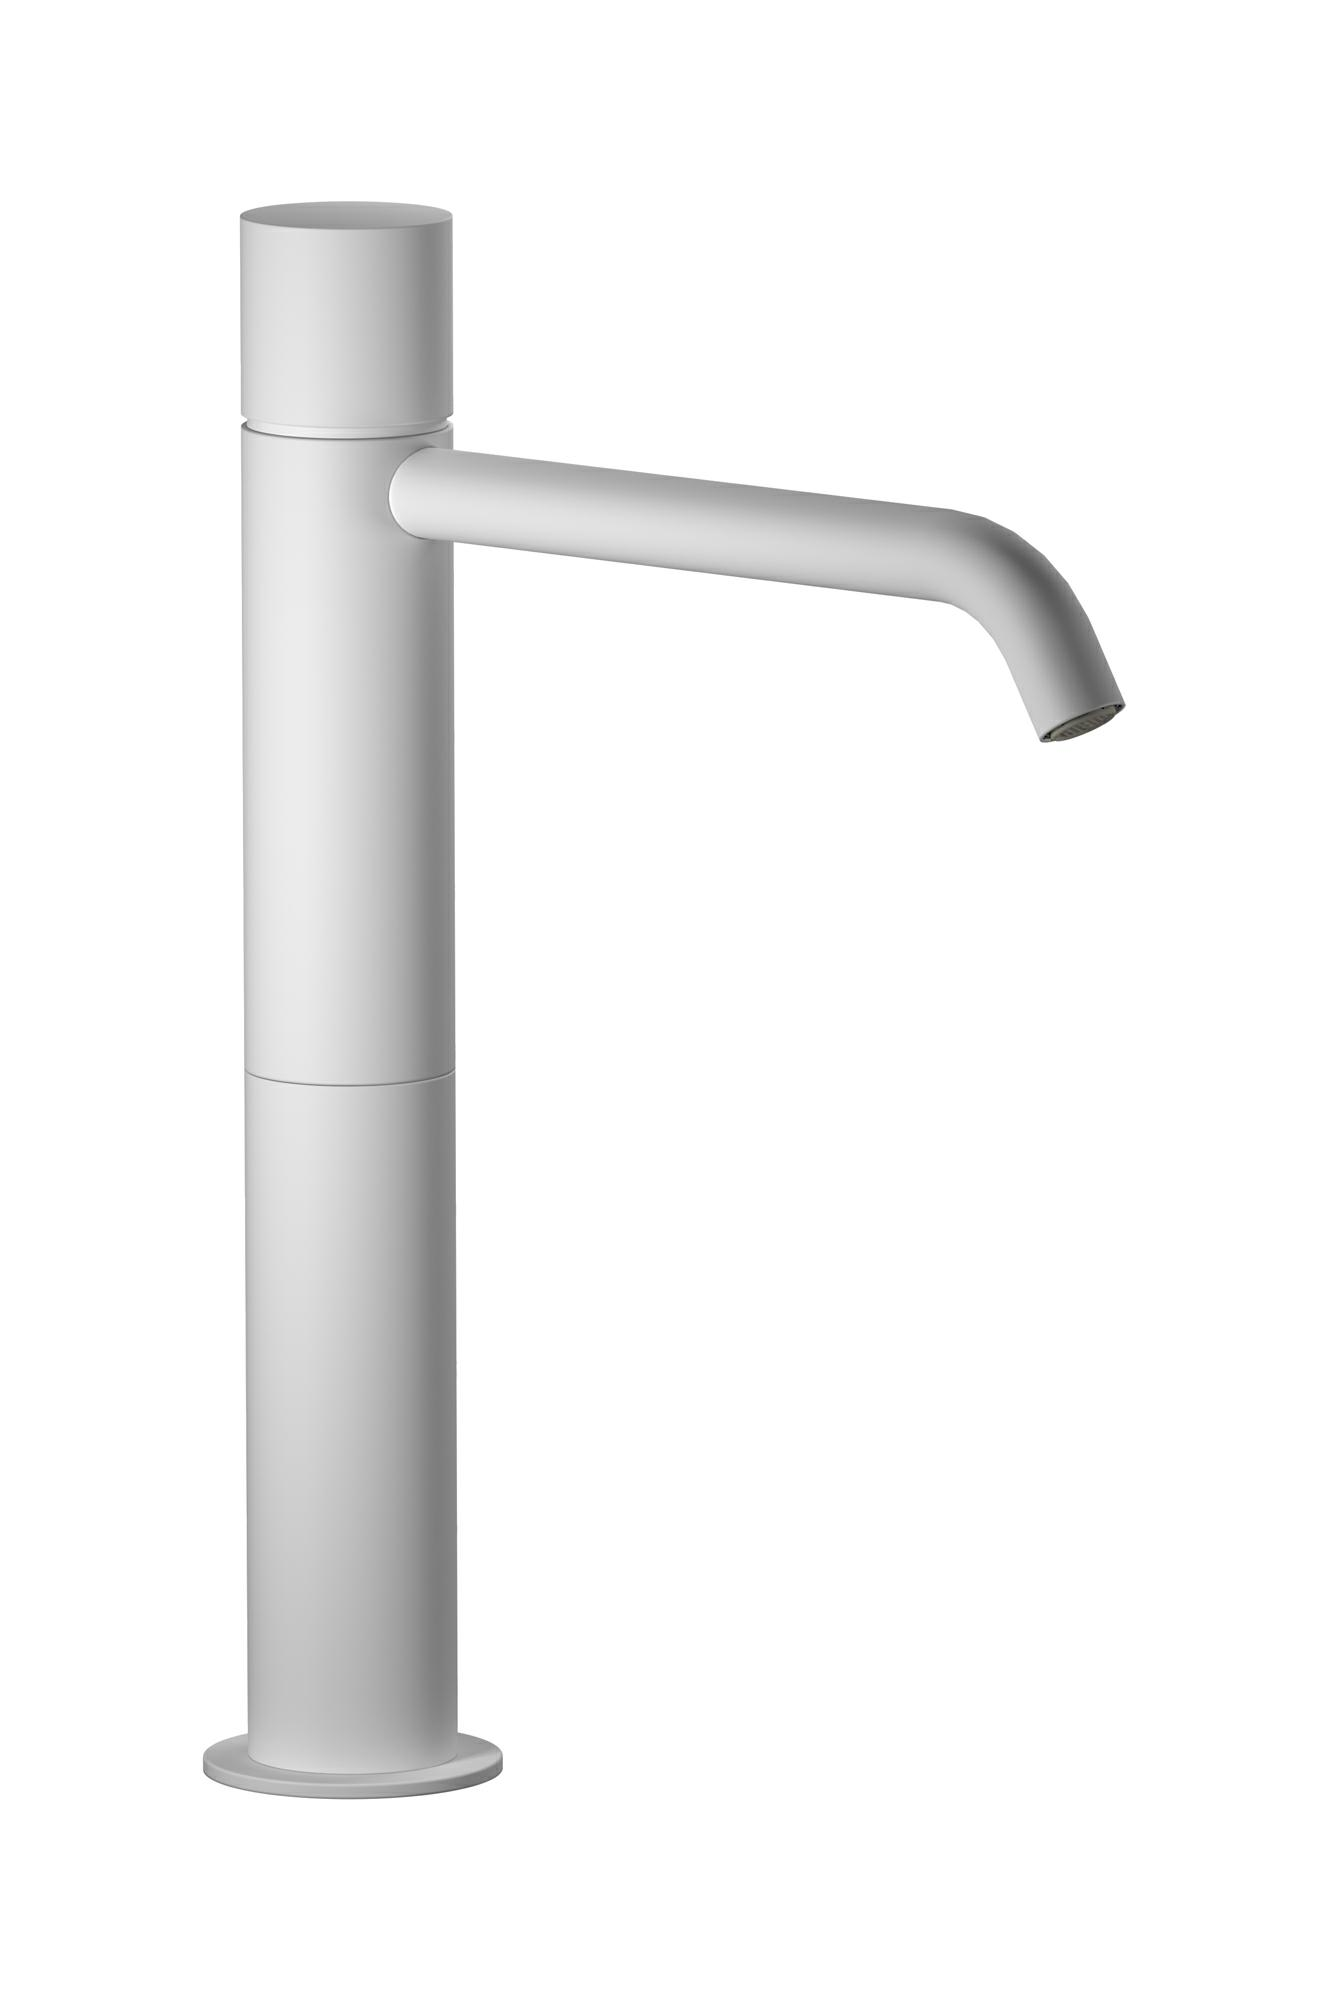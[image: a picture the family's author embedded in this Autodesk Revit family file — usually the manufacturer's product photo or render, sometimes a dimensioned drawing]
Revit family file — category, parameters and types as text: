
# Revit family: RR370
name_source: partatom
category: Apparecchi idraulici
units: mm (PartAtom-declared; Revit-internal decimal feet)

## family parameters
Basato su piano di lavoro = No
Condiviso = No
Mantieni orientamento annotazione = No
Numero OmniClass = 23.45.55.17
Punto di calcolo locali = No
Quota connettore circolare = Usa diametro
Sempre verticale = Sì
Taglio con vuoti quando caricato = No
Tipo di parte = Normale
Titolo OmniClass = Mixing Faucets

## types (13) — shared parameters
Cold water inlet = 10 mm  [stored 0.0328084 ft]
Commenti sul tipo = Single lever kitchen mixer
Connessione CW = No
Connessione HW = No
Connessione di scarico = No
Connessione di ventilazione = No
Descrizione = Single lever kitchen mixer
Hot water inlet = 10 mm  [stored 0.0328084 ft]
Produttore = IB Rubinetterie S.p.A.
URL = https://www.weareib.it
zero-valued in all types: Prospetto di default

## per-type parameters (varying)
| type | Finishes surface | Immagine tipo | Modello |
| Chrome | IB_Chrome | RR370CC.jpg | RR370CC |
| Matt White | IB_matt white | RR370BO.jpg | RR370BO |
| Black Chrome | IB_Black chrome | RR370CF.jpg | RR370CF |
| Brushed Black Chrome | IB_Brushed black chrome | RR370CS.jpg | RR370CS |
| Pale Gold | IB_Pale gold | RR370II.jpg | RR370II |
| Brushed Pale Gold | IB_brushed pale gold | RR370IS.jpg | RR370IS |
| Modern Bronze | IB_Modern bronze | RR370MB.jpg | RR370MB |
| Matt Black | IB_matt black | RR370NP.jpg | RR370NP |
| Gold | IB_gold | RR370OO.jpg | RR370OO |
| Brushed Gold | IB_brushed gold | RR370OS.jpg | RR370OS |
| Rose Gold | IB_Rose gold | RR370RS.jpg | RR370RS |
| Brushed Rose Gold | IB_Brushed rose gold | RR370SR.jpg | RR370SR |
| Brushed Nickel | IB_Brushed nickel | RR370SS.jpg | RR370SS |

note: [stored X ft] marks values corroborated as IEEE doubles in the binary element streams (Revit-internal decimal feet)
